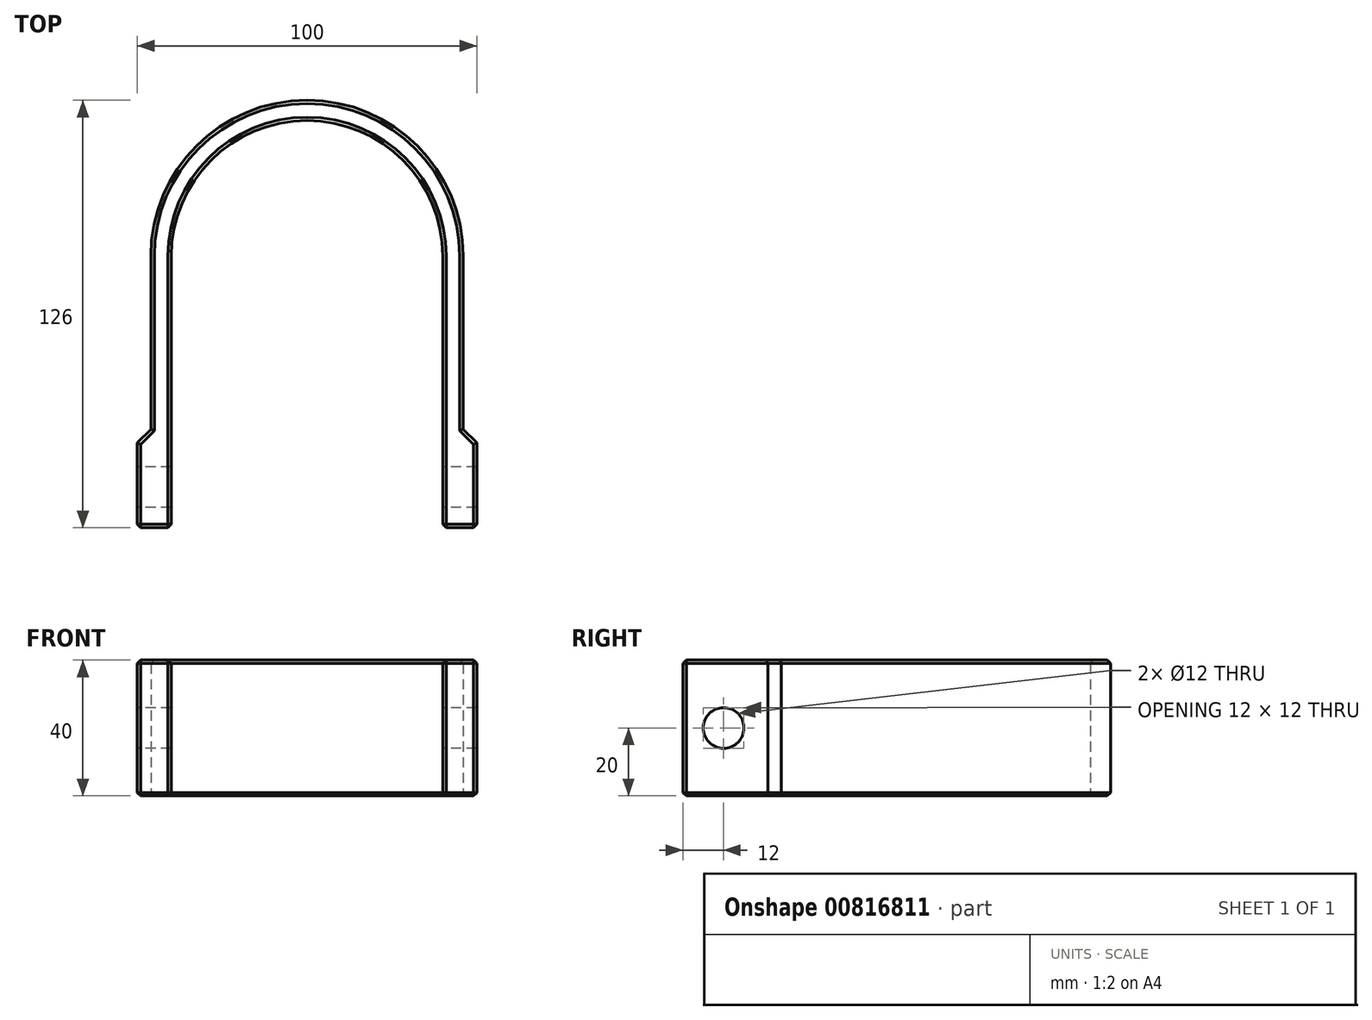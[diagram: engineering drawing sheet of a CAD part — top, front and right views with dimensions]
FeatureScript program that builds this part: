
annotation { "Feature Type Name" : "Feature", "Feature Type Description" : "" }
export const myFeature = defineFeature(function(context is Context, id is Id, definition is map)
    precondition{}
    {
        {
            var Q0;
            Q0=qCreatedBy(makeId("Top.planeOp"),FACE);
            var sketch = newSketch(context, id + "F0", { "sketchPlane" : qUnion([Q0])});
            skArc(sketch, "E0", {"start": v(40, 0) * mm, "mid": v(0, 40) * mm, "end": v(-40, 0) * mm});
            skArc(sketch, "E1", {"start": v(46, 0) * mm, "mid": v(0, 46) * mm, "end": v(-46, 0) * mm});
            skLineSegment(sketch, "E2", {"start": v(40, 0) * mm, "end": v(40, -80) * mm});
            skLineSegment(sketch, "E3", {"start": v(-40, 0) * mm, "end": v(-40, -80) * mm});
            skLineSegment(sketch, "E4", {"start": v(40, -80) * mm, "end": v(50, -80) * mm});
            skLineSegment(sketch, "E5", {"start": v(50, -80) * mm, "end": v(50, -55) * mm});
            skLineSegment(sketch, "E6", {"start": v(50, -55) * mm, "end": v(46, -51) * mm});
            skLineSegment(sketch, "E7", {"start": v(46, -51) * mm, "end": v(46, 0) * mm});
            skLineSegment(sketch, "E8.MirrorCS", {"start": v(-40, -80) * mm, "end": v(-50, -80) * mm});
            skLineSegment(sketch, "E9.MirrorCS", {"start": v(-50, -80) * mm, "end": v(-50, -55) * mm});
            skLineSegment(sketch, "E10.MirrorCS", {"start": v(-46, -51) * mm, "end": v(-46, 0) * mm});
            skLineSegment(sketch, "E11.MirrorCS", {"start": v(-50, -55) * mm, "end": v(-46, -51) * mm});
            skSolve(sketch);
        }
        {
            var Q0;
            Q0=makeQuery(id+"F0.imprint","IMPRINT",FACE,{"disambiguationData":[TD([[makeQuery(id+"F0.imprint","IMPRINT",EDGE,{"derivedFrom":sQuery(id+"F0.wireOp",EDGE,"E0")}),-1.0]])]});
            extrude(context, id + "F1", {"entities" : qUnion([Q0]), "depth" : 40 * mm, "offsetDistance" : 25 * mm});
        }
        {
            var Q0;
            Q0=makeQuery(id+"F1.opExtrude","SWEPT_FACE",FACE,{"disambiguationData":[OSD([sQuery(id+"F0.wireOp",EDGE,"E9.MirrorCS")])]});
            var sketch = newSketch(context, id + "F2", { "sketchPlane" : qUnion([Q0])});
            skPoint(sketch, "E12", {"position": v(68, 20) * mm});
            skSolve(sketch);
        }
        {
            var Q0;
            Q0=sQuery(id+"F2.wireOp",VERTEX,"E12");
            var Q1;
            Q1=makeQuery(id+"F1.opExtrude","SWEPT_BODY",BODY,{"disambiguationData":[OSD([sQuery(id+"F0.wireOp",EDGE,"E0"),sQuery(id+"F0.wireOp",EDGE,"E1"),sQuery(id+"F0.wireOp",EDGE,"E2"),sQuery(id+"F0.wireOp",EDGE,"E3"),sQuery(id+"F0.wireOp",EDGE,"E4"),sQuery(id+"F0.wireOp",EDGE,"E5"),sQuery(id+"F0.wireOp",EDGE,"E6"),sQuery(id+"F0.wireOp",EDGE,"E7"),sQuery(id+"F0.wireOp",EDGE,"E8.MirrorCS"),sQuery(id+"F0.wireOp",EDGE,"E9.MirrorCS"),sQuery(id+"F0.wireOp",EDGE,"E10.MirrorCS"),sQuery(id+"F0.wireOp",EDGE,"E11.MirrorCS")])]});
            hole(context, id + "F3", {"style" : HoleStyle.SIMPLE, "endStyle" : HoleEndStyle.THROUGH, "holeDiameter" : 12 * mm, "majorDiameter" : 5 * mm, "isTappedThrough" : true, "tappedDepth" : 12 * mm, "tapClearance" : 3, "locations" : qUnion([Q0]), "scope" : qUnion([Q1])});
        }
        {
            var Q0;
            Q0=makeQuery(id+"F1.opExtrude","CAP_EDGE",EDGE,{"disambiguationData":[OSD([sQuery(id+"F0.wireOp",EDGE,"E2")])],"isStart":false});
            var Q1;
            Q1=makeQuery(id+"F1.opExtrude","CAP_EDGE",EDGE,{"disambiguationData":[OSD([sQuery(id+"F0.wireOp",EDGE,"E3")])],"isStart":true});
            var Q2;
            Q2=makeQuery(id+"F1.opExtrude","SWEPT_EDGE",EDGE,{"disambiguationData":[OSD([sQuery(id+"F0.wireOp",EDGE,"E2"),sQuery(id+"F0.wireOp",EDGE,"E4")])]});
            var Q3;
            Q3=makeQuery(id+"F1.opExtrude","SWEPT_EDGE",EDGE,{"disambiguationData":[OSD([sQuery(id+"F0.wireOp",EDGE,"E3"),sQuery(id+"F0.wireOp",EDGE,"E8.MirrorCS")])]});
            var Q4;
            Q4=makeQuery(id+"F1.opExtrude","SWEPT_EDGE",EDGE,{"disambiguationData":[OSD([sQuery(id+"F0.wireOp",EDGE,"E8.MirrorCS"),sQuery(id+"F0.wireOp",EDGE,"E9.MirrorCS")])]});
            var Q5;
            Q5=makeQuery(id+"F1.opExtrude","CAP_EDGE",EDGE,{"disambiguationData":[OSD([sQuery(id+"F0.wireOp",EDGE,"E8.MirrorCS")])],"isStart":true});
            var Q6;
            Q6=makeQuery(id+"F1.opExtrude","CAP_EDGE",EDGE,{"disambiguationData":[OSD([sQuery(id+"F0.wireOp",EDGE,"E8.MirrorCS")])],"isStart":false});
            var Q7;
            Q7=makeQuery(id+"F1.opExtrude","CAP_EDGE",EDGE,{"disambiguationData":[OSD([sQuery(id+"F0.wireOp",EDGE,"E4")])],"isStart":false});
            var Q8;
            Q8=makeQuery(id+"F1.opExtrude","SWEPT_EDGE",EDGE,{"disambiguationData":[OSD([sQuery(id+"F0.wireOp",EDGE,"E4"),sQuery(id+"F0.wireOp",EDGE,"E5")])]});
            var Q9;
            Q9=makeQuery(id+"F1.opExtrude","CAP_EDGE",EDGE,{"disambiguationData":[OSD([sQuery(id+"F0.wireOp",EDGE,"E4")])],"isStart":true});
            var Q10;
            Q10=makeQuery(id+"F1.opExtrude","CAP_EDGE",EDGE,{"disambiguationData":[OSD([sQuery(id+"F0.wireOp",EDGE,"E5")])],"isStart":true});
            var Q11;
            Q11=makeQuery(id+"F1.opExtrude","CAP_EDGE",EDGE,{"disambiguationData":[OSD([sQuery(id+"F0.wireOp",EDGE,"E5")])],"isStart":false});
            var Q12;
            Q12=makeQuery(id+"F1.opExtrude","CAP_EDGE",EDGE,{"disambiguationData":[OSD([sQuery(id+"F0.wireOp",EDGE,"E9.MirrorCS")])],"isStart":false});
            var Q13;
            Q13=makeQuery(id+"F1.opExtrude","CAP_EDGE",EDGE,{"disambiguationData":[OSD([sQuery(id+"F0.wireOp",EDGE,"E9.MirrorCS")])],"isStart":true});
            var Q14;
            Q14=makeQuery(id+"F1.opExtrude","CAP_EDGE",EDGE,{"disambiguationData":[OSD([sQuery(id+"F0.wireOp",EDGE,"E10.MirrorCS")])],"isStart":true});
            var Q15;
            Q15=makeQuery(id+"F1.opExtrude","CAP_EDGE",EDGE,{"disambiguationData":[OSD([sQuery(id+"F0.wireOp",EDGE,"E10.MirrorCS")])],"isStart":false});
            var Q16;
            Q16=makeQuery(id+"F1.opExtrude","CAP_EDGE",EDGE,{"disambiguationData":[OSD([sQuery(id+"F0.wireOp",EDGE,"E11.MirrorCS")])],"isStart":false});
            var Q17;
            Q17=makeQuery(id+"F1.opExtrude","CAP_EDGE",EDGE,{"disambiguationData":[OSD([sQuery(id+"F0.wireOp",EDGE,"E11.MirrorCS")])],"isStart":true});
            var Q18;
            Q18=makeQuery(id+"F1.opExtrude","CAP_EDGE",EDGE,{"disambiguationData":[OSD([sQuery(id+"F0.wireOp",EDGE,"E6")])],"isStart":true});
            var Q19;
            Q19=makeQuery(id+"F1.opExtrude","CAP_EDGE",EDGE,{"disambiguationData":[OSD([sQuery(id+"F0.wireOp",EDGE,"E6")])],"isStart":false});
            chamfer(context, id + "F4", {"entities" : qUnion([Q0, Q1, Q2, Q3, Q4, Q5, Q6, Q7, Q8, Q9, Q10, Q11, Q12, Q13, Q14, Q15, Q16, Q17, Q18, Q19]), "width" : 1 * mm, "tangentPropagation" : true});
        }
    });
